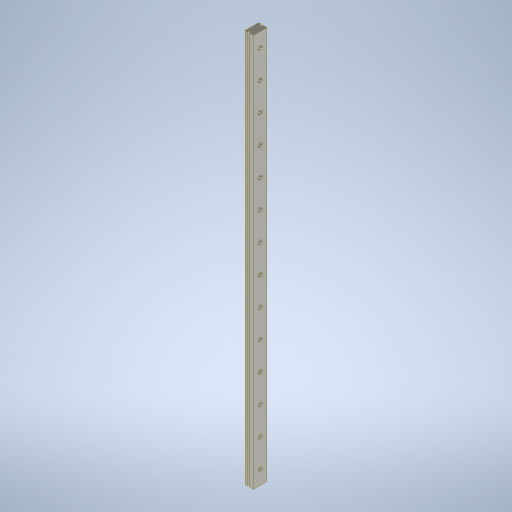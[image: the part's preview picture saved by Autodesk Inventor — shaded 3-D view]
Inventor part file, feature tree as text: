
AUTODESK INVENTOR PART (.ipt)
format: ipt  version: 2023 (Build 270158000, 158)  size: 303,104 bytes
history: native  units: mm
features: sketch x2, other x1, extrude x1, hole x1
ambient origin geometry x8: Origin, YZ Plane, XZ Plane, XY Plane, X Axis, Y Axis, Z Axis, Center Point
bodies: Body1 (feature_tree)
feature tree (5):
  other  "Sólido1"
  extrude  "Extrusão1"  Depth=12.0mm
  hole  "Furo1"  [1 undecoded]
  sketch  "Esboço1"  dims[d0=7.5mm d1=12.0mm]
  sketch  "Esboço2"  dims[d2=8.0mm d3=1.0mm d4=3.5mm d5=0.5mm d6=350.0mm d7=0.0mm d8=25.0mm d9=12.5mm d10=12.0mm d11=6.0mm d12=6.0mm d13=25.0mm d14=25.0mm d15=25.0mm d16=25.0mm d17=25.0mm d18=25.0mm d19=25.0mm d20=25.0mm d21=25.0mm d22=25.0mm d23=25.0mm d24=25.0mm d25=12.5mm d26=3.5mm d27=7.0mm d28=6.0mm d29=3.5mm d30=90.0deg d31=0.5mm d32=20.594885mm]
note: 1 required parameter value undecoded (feature->parameter linkage not recoverable at this tier; creation-order binding heuristic only, values carry confidence <= 0.55)
